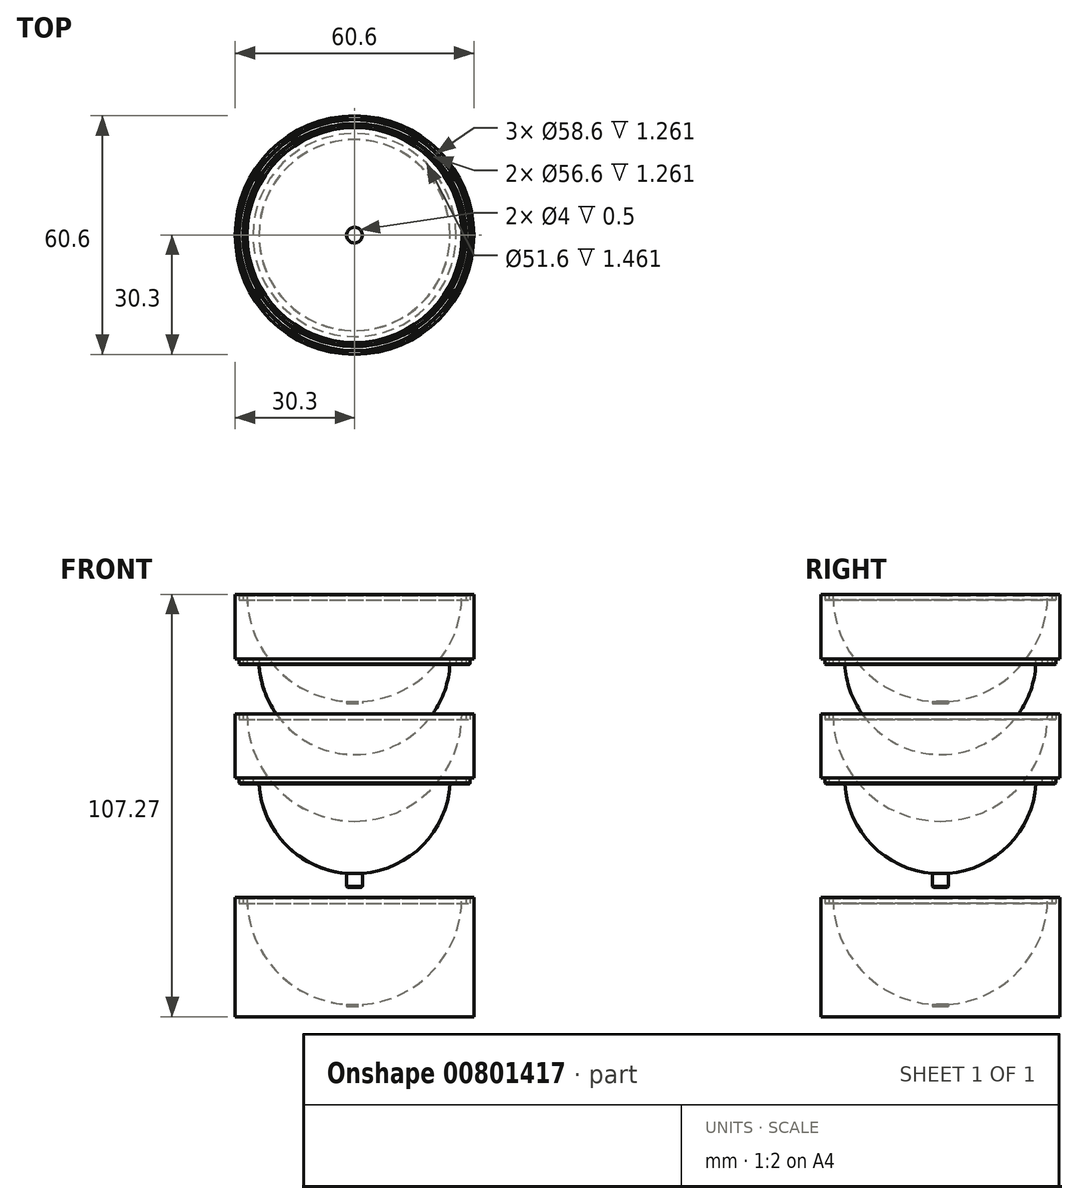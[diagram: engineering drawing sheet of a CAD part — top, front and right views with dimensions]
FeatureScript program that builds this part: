
annotation { "Feature Type Name" : "Feature", "Feature Type Description" : "" }
export const myFeature = defineFeature(function(context is Context, id is Id, definition is map)
    precondition{}
    {
        {
            var Q0;
            Q0=qCreatedBy(makeId("Front.planeOp"),FACE);
            var sketch = newSketch(context, id + "F0", { "sketchPlane" : qUnion([Q0])});
            skLineSegment(sketch, "E0.bottom", {"start": v(0, 0) * mm, "end": v(-30.3, 0) * mm});
            skLineSegment(sketch, "E0.top", {"start": v(0, 30.3) * mm, "end": v(-30.3, 30.3) * mm});
            skLineSegment(sketch, "E0.left", {"start": v(0, 0) * mm, "end": v(0, 30.3) * mm});
            skLineSegment(sketch, "E0.right", {"start": v(-30.3, 0) * mm, "end": v(-30.3, 30.3) * mm});
            skArc(sketch, "E1", {"start": v(-27.3, 30.3) * mm, "mid": v(-19.3, 11) * mm, "end": v(0, 3) * mm});
            skLineSegment(sketch, "E2", {"start": v(0, 3) * mm, "end": v(-27.3, 3) * mm, "construction": true});
            skLineSegment(sketch, "E3", {"start": v(-27.3, 3) * mm, "end": v(-27.3, 30.3) * mm, "construction": true});
            skArc(sketch, "E4", {"start": v(-24.3, 30.3) * mm, "mid": v(-17.18, 13.12) * mm, "end": v(0, 6) * mm});
            skLineSegment(sketch, "E5", {"start": v(-25.8, 30.3) * mm, "end": v(-25.8, 28.84) * mm});
            skLineSegment(sketch, "E6", {"start": v(-25.8, 28.84) * mm, "end": v(-27.26, 28.84) * mm});
            skLineSegment(sketch, "E7", {"start": v(-27.3, 30.3) * mm, "end": v(-27.3, 46.67) * mm, "construction": true});
            skArc(sketch, "E8", {"start": v(-27.3, 46.67) * mm, "mid": v(-19.3, 27.37) * mm, "end": v(0, 19.37) * mm});
            skLineSegment(sketch, "E9", {"start": v(-30.3, 30.3) * mm, "end": v(-30.3, 46.67) * mm});
            skLineSegment(sketch, "E10", {"start": v(-30.3, 46.67) * mm, "end": v(-27.3, 46.67) * mm});
            skLineSegment(sketch, "E11", {"start": v(-27.3, 46.67) * mm, "end": v(0, 46.67) * mm});
            skLineSegment(sketch, "E12", {"start": v(-25.8, 28.84) * mm, "end": v(-24.26, 28.84) * mm});
            skArc(sketch, "E13", {"start": v(-24.3, 46.67) * mm, "mid": v(-17.18, 29.49) * mm, "end": v(0, 22.37) * mm});
            skLineSegment(sketch, "E14", {"start": v(-25.8, 46.67) * mm, "end": v(-25.8, 45.2) * mm});
            skLineSegment(sketch, "E15", {"start": v(-25.8, 45.2) * mm, "end": v(-27.26, 45.2) * mm});
            skLineSegment(sketch, "E16", {"start": v(-25.8, 45.2) * mm, "end": v(-24.26, 45.2) * mm});
            skLineSegment(sketch, "E17.bottom", {"start": v(-29.3, 30.3) * mm, "end": v(-28.3, 30.3) * mm});
            skLineSegment(sketch, "E17.top", {"start": v(-29.3, 28.84) * mm, "end": v(-28.3, 28.84) * mm});
            skLineSegment(sketch, "E17.left", {"start": v(-29.3, 28.84) * mm, "end": v(-29.3, 30.3) * mm});
            skLineSegment(sketch, "E17.right", {"start": v(-28.3, 28.84) * mm, "end": v(-28.3, 30.3) * mm});
            skLineSegment(sketch, "E18", {"start": v(-28.8, 30.3) * mm, "end": v(-28.8, 28.84) * mm, "construction": true});
            skPoint(sketch, "E19", {"position": v(-28.8, 28.84) * mm});
            skPoint(sketch, "E20", {"position": v(-26.53, 28.84) * mm});
            skLineSegment(sketch, "E21", {"start": v(-28.8, 46.67) * mm, "end": v(-28.8, 45.2) * mm, "construction": true});
            skLineSegment(sketch, "E22.bottom", {"start": v(-29.3, 46.67) * mm, "end": v(-28.3, 46.67) * mm});
            skLineSegment(sketch, "E22.top", {"start": v(-29.3, 45.2) * mm, "end": v(-28.3, 45.2) * mm});
            skLineSegment(sketch, "E22.left", {"start": v(-29.3, 46.67) * mm, "end": v(-29.3, 45.2) * mm});
            skLineSegment(sketch, "E22.right", {"start": v(-28.3, 46.67) * mm, "end": v(-28.3, 45.2) * mm});
            skLineSegment(sketch, "E23", {"start": v(-2, 22.45) * mm, "end": v(-2, 19.44) * mm});
            skLineSegment(sketch, "E24", {"start": v(-2, 6.08) * mm, "end": v(-2, 3.07) * mm});
            skLineSegment(sketch, "E25", {"start": v(-2, 19.44) * mm, "end": v(-2, 18.94) * mm});
            skLineSegment(sketch, "E26", {"start": v(-2, 18.94) * mm, "end": v(0, 18.94) * mm});
            skLineSegment(sketch, "E27", {"start": v(-2, 3.07) * mm, "end": v(-2, 2.57) * mm});
            skLineSegment(sketch, "E28", {"start": v(-2, 2.57) * mm, "end": v(0, 2.57) * mm});
            skSolve(sketch);
        }
        {
            var Q0;
            {var subQ6=sQuery(id+"F0.wireOp",EDGE,"E0.bottom");Q0=makeQuery(id+"F0.imprint","IMPRINT",FACE,{"disambiguationData":[TD([[makeQuery(id+"F0.imprint","IMPRINT",EDGE,{"derivedFrom":subQ6}),-1.0]])]});}
            var Q1;
            Q1=sQuery(id+"F0.wireOp",EDGE,"E0.left");
            revolve(context, id + "F1", {"surfaceOperationType" : NewSurfaceOperationType.NEW, "entities" : qUnion([Q0]), "axis" : qUnion([Q1]), "revolveType" : RevolveType.FULL});
        }
        {
            var Q0;
            {var subQ1=sQuery(id+"F0.wireOp",EDGE,"E9");Q0=makeQuery(id+"F0.imprint","IMPRINT",FACE,{"disambiguationData":[TD([[makeQuery(id+"F0.imprint","IMPRINT",EDGE,{"derivedFrom":subQ1}),-1.0]])]});}
            var Q1;
            {var subQ10=sQuery(id+"F0.wireOp",EDGE,"E25");Q1=makeQuery(id+"F0.imprint","IMPRINT",FACE,{"disambiguationData":[TD([[makeQuery(id+"F0.imprint","IMPRINT",EDGE,{"derivedFrom":subQ10}),-1.0]])]});}
            var Q2;
            {var subQ5=sQuery(id+"F0.wireOp",EDGE,"E24");Q2=makeQuery(id+"F0.imprint","IMPRINT",FACE,{"disambiguationData":[TD([[makeQuery(id+"F0.imprint","IMPRINT",EDGE,{"derivedFrom":subQ5}),1.0]])]});}
            var Q3;
            {var subQ4=sQuery(id+"F0.wireOp",EDGE,"E27");Q3=makeQuery(id+"F0.imprint","IMPRINT",FACE,{"disambiguationData":[TD([[makeQuery(id+"F0.imprint","IMPRINT",EDGE,{"derivedFrom":subQ4}),1.0]])]});}
            var Q4;
            {var subQ3=sQuery(id+"F0.wireOp",EDGE,"E5");Q4=makeQuery(id+"F0.imprint","IMPRINT",FACE,{"disambiguationData":[TD([[makeQuery(id+"F0.imprint","IMPRINT",EDGE,{"derivedFrom":subQ3}),1.0]])]});}
            var Q5;
            Q5=makeQuery(id+"F0.imprint","IMPRINT",FACE,{"disambiguationData":[TD([[makeQuery(id+"F0.imprint","IMPRINT",EDGE,{"derivedFrom":sQuery(id+"F0.wireOp",EDGE,"E17.top")}),1.0]])]});
            var Q6;
            {var subQ4=sQuery(id+"F0.wireOp",EDGE,"E25");Q6=makeQuery(id+"F0.imprint","IMPRINT",FACE,{"disambiguationData":[TD([[makeQuery(id+"F0.imprint","IMPRINT",EDGE,{"derivedFrom":subQ4}),1.0]])]});}
            var Q7;
            Q7=sQuery(id+"F0.wireOp",EDGE,"E0.left");
            revolve(context, id + "F2", {"surfaceOperationType" : NewSurfaceOperationType.NEW, "entities" : qUnion([Q0, Q1, Q2, Q3, Q4, Q5, Q6]), "axis" : qUnion([Q7]), "revolveType" : RevolveType.FULL});
        }
        {
            var Q0;
            {var subQ10=sQuery(id+"F0.wireOp",EDGE,"E25");Q0=makeQuery(id+"F0.imprint","IMPRINT",FACE,{"disambiguationData":[TD([[makeQuery(id+"F0.imprint","IMPRINT",EDGE,{"derivedFrom":subQ10}),-1.0]])]});}
            var Q1;
            {var subQ1=sQuery(id+"F0.wireOp",EDGE,"E9");Q1=makeQuery(id+"F0.imprint","IMPRINT",FACE,{"disambiguationData":[TD([[makeQuery(id+"F0.imprint","IMPRINT",EDGE,{"derivedFrom":subQ1}),-1.0]])]});}
            var Q2;
            Q2=makeQuery(id+"F0.imprint","IMPRINT",FACE,{"disambiguationData":[TD([[makeQuery(id+"F0.imprint","IMPRINT",EDGE,{"derivedFrom":sQuery(id+"F0.wireOp",EDGE,"E17.top")}),1.0]])]});
            var Q3;
            {var subQ3=sQuery(id+"F0.wireOp",EDGE,"E5");Q3=makeQuery(id+"F0.imprint","IMPRINT",FACE,{"disambiguationData":[TD([[makeQuery(id+"F0.imprint","IMPRINT",EDGE,{"derivedFrom":subQ3}),-1.0]])]});}
            var Q4;
            Q4=sQuery(id+"F0.wireOp",EDGE,"E0.left");
            revolve(context, id + "F3", {"surfaceOperationType" : NewSurfaceOperationType.NEW, "entities" : qUnion([Q0, Q1, Q2, Q3]), "axis" : qUnion([Q4]), "revolveType" : RevolveType.FULL});
        }
        {
            var Q0;
            Q0=makeQuery(id+"F1.opRevolve","SWEPT_BODY",BODY,{"disambiguationData":[OSD([sQuery(id+"F0.wireOp",EDGE,"E0.bottom"),sQuery(id+"F0.wireOp",EDGE,"E0.top"),sQuery(id+"F0.wireOp",EDGE,"E0.left"),sQuery(id+"F0.wireOp",EDGE,"E0.right"),sQuery(id+"F0.wireOp",EDGE,"E1"),sQuery(id+"F0.wireOp",EDGE,"E17.top"),sQuery(id+"F0.wireOp",EDGE,"E17.left"),sQuery(id+"F0.wireOp",EDGE,"E17.right"),sQuery(id+"F0.wireOp",EDGE,"E27"),sQuery(id+"F0.wireOp",EDGE,"E28")])]});
            var Q1;
            Q1=sQuery(id+"F0.wireOp",EDGE,"E0.left");
            transform(context, id + "F4", {"entities" : qUnion([Q0]), "transformType" : TransformType.TRANSLATION_ENTITY, "oppositeDirectionEntity" : true, "transformLine" : qUnion([Q1]), "makeCopy" : false});
        }
        {
            var Q0;
            Q0=makeQuery(id+"F3.opRevolve","SWEPT_BODY",BODY,{"disambiguationData":[OSD([sQuery(id+"F0.wireOp",EDGE,"E0.top"),sQuery(id+"F0.wireOp",EDGE,"E0.left"),sQuery(id+"F0.wireOp",EDGE,"E1"),sQuery(id+"F0.wireOp",EDGE,"E4"),sQuery(id+"F0.wireOp",EDGE,"E5"),sQuery(id+"F0.wireOp",EDGE,"E6"),sQuery(id+"F0.wireOp",EDGE,"E8"),sQuery(id+"F0.wireOp",EDGE,"E9"),sQuery(id+"F0.wireOp",EDGE,"E10"),sQuery(id+"F0.wireOp",EDGE,"E17.top"),sQuery(id+"F0.wireOp",EDGE,"E17.left"),sQuery(id+"F0.wireOp",EDGE,"E17.right"),sQuery(id+"F0.wireOp",EDGE,"E22.top"),sQuery(id+"F0.wireOp",EDGE,"E22.left"),sQuery(id+"F0.wireOp",EDGE,"E22.right"),sQuery(id+"F0.wireOp",EDGE,"E25"),sQuery(id+"F0.wireOp",EDGE,"E26")])]});
            var Q1;
            Q1=sQuery(id+"F0.wireOp",EDGE,"E0.left");
            transform(context, id + "F5", {"entities" : qUnion([Q0]), "transformType" : TransformType.TRANSLATION_ENTITY, "oppositeDirectionEntity" : false, "transformLine" : qUnion([Q1]), "makeCopy" : false});
        }
        {
            var Q0;
            Q0=makeQuery(id+"F2.opRevolve","SWEPT_EDGE",EDGE,{"disambiguationData":[OSD([sQuery(id+"F0.wireOp",EDGE,"E17.top"),sQuery(id+"F0.wireOp",EDGE,"E17.left")])]});
            var Q1;
            Q1=makeQuery(id+"F2.opRevolve","SWEPT_EDGE",EDGE,{"disambiguationData":[OSD([sQuery(id+"F0.wireOp",EDGE,"E17.top"),sQuery(id+"F0.wireOp",EDGE,"E17.right")])]});
            var Q2;
            Q2=makeQuery(id+"F2.opRevolve","SWEPT_EDGE",EDGE,{"disambiguationData":[OSD([sQuery(id+"F0.wireOp",EDGE,"E10"),sQuery(id+"F0.wireOp",EDGE,"E22.left")])]});
            var Q3;
            Q3=makeQuery(id+"F2.opRevolve","SWEPT_EDGE",EDGE,{"disambiguationData":[OSD([sQuery(id+"F0.wireOp",EDGE,"E10"),sQuery(id+"F0.wireOp",EDGE,"E22.right")])]});
            chamfer(context, id + "F6", {"entities" : qUnion([Q0, Q1, Q2, Q3]), "width" : .2 * mm, "tangentPropagation" : true});
        }
        {
            var Q0;
            Q0=makeQuery(id+"F3.opRevolve","SWEPT_EDGE",EDGE,{"disambiguationData":[OSD([sQuery(id+"F0.wireOp",EDGE,"E10"),sQuery(id+"F0.wireOp",EDGE,"E22.left")])]});
            var Q1;
            Q1=makeQuery(id+"F3.opRevolve","SWEPT_EDGE",EDGE,{"disambiguationData":[OSD([sQuery(id+"F0.wireOp",EDGE,"E10"),sQuery(id+"F0.wireOp",EDGE,"E22.right")])]});
            var Q2;
            Q2=makeQuery(id+"F3.opRevolve","SWEPT_EDGE",EDGE,{"disambiguationData":[OSD([sQuery(id+"F0.wireOp",EDGE,"E17.top"),sQuery(id+"F0.wireOp",EDGE,"E17.left")])]});
            var Q3;
            Q3=makeQuery(id+"F3.opRevolve","SWEPT_EDGE",EDGE,{"disambiguationData":[OSD([sQuery(id+"F0.wireOp",EDGE,"E17.top"),sQuery(id+"F0.wireOp",EDGE,"E17.right")])]});
            chamfer(context, id + "F7", {"entities" : qUnion([Q0, Q1, Q2, Q3]), "width" : .2 * mm, "tangentPropagation" : true});
        }
        {
            var Q0;
            Q0=makeQuery(id+"F1.opRevolve","SWEPT_EDGE",EDGE,{"disambiguationData":[OSD([sQuery(id+"F0.wireOp",EDGE,"E0.top"),sQuery(id+"F0.wireOp",EDGE,"E17.right")])]});
            var Q1;
            Q1=makeQuery(id+"F1.opRevolve","SWEPT_EDGE",EDGE,{"disambiguationData":[OSD([sQuery(id+"F0.wireOp",EDGE,"E0.top"),sQuery(id+"F0.wireOp",EDGE,"E17.left")])]});
            chamfer(context, id + "F8", {"entities" : qUnion([Q0, Q1]), "width" : .2 * mm, "tangentPropagation" : true});
        }
        {
            var Q0;
            Q0=makeQuery(id+"F2.opRevolve","SWEPT_EDGE",EDGE,{"disambiguationData":[OSD([sQuery(id+"F0.wireOp",EDGE,"E27"),sQuery(id+"F0.wireOp",EDGE,"E28")])]});
            chamfer(context, id + "F9", {"entities" : qUnion([Q0]), "width" : .2 * mm, "tangentPropagation" : true});
        }
    });
